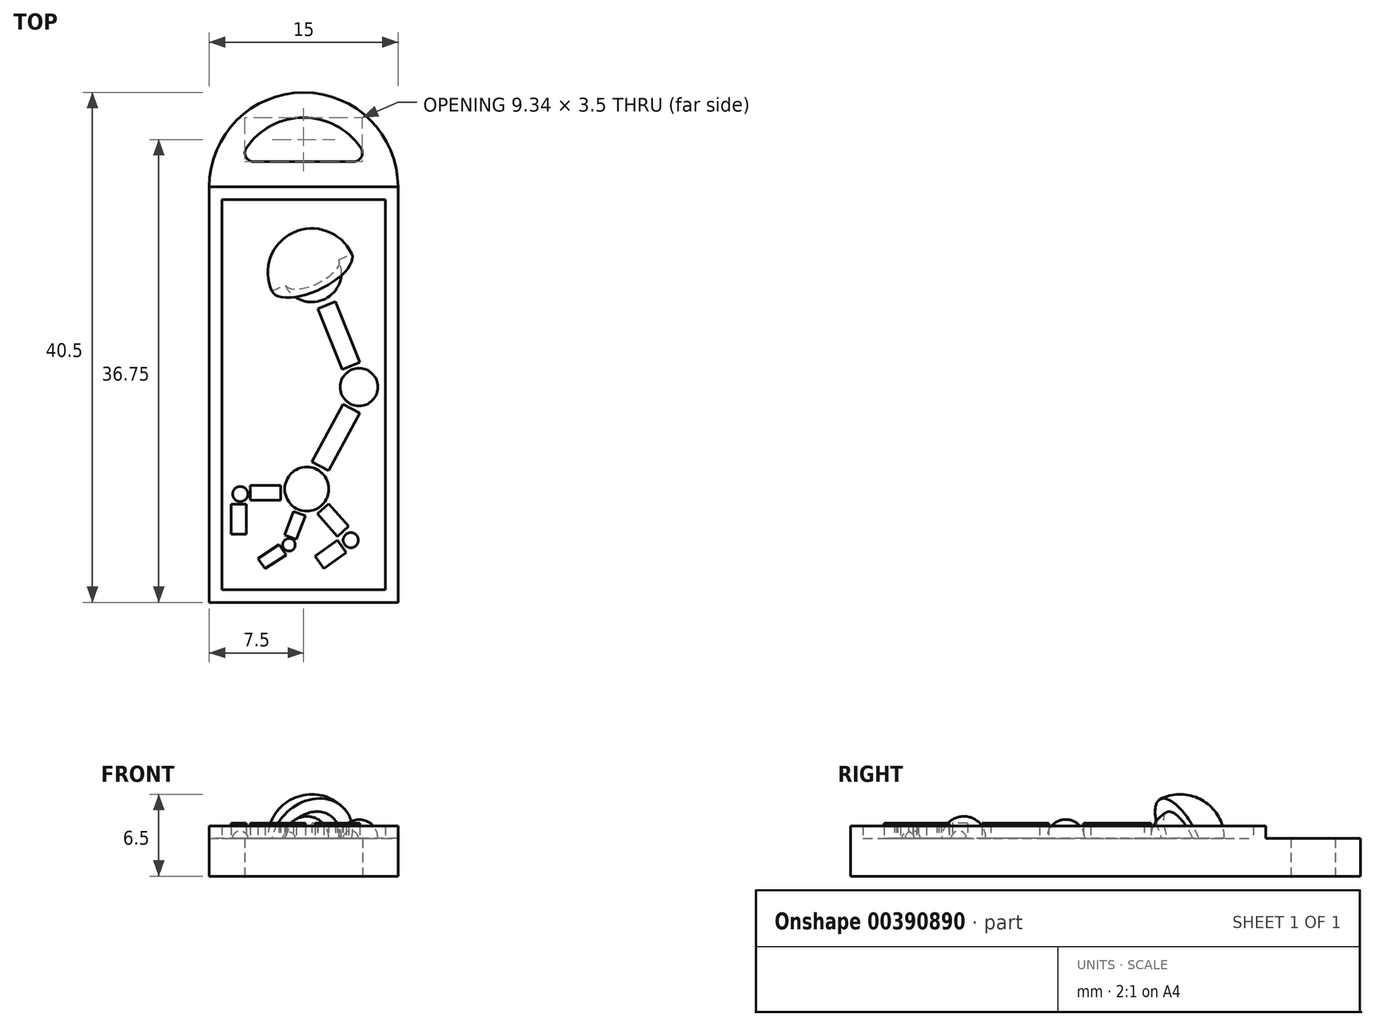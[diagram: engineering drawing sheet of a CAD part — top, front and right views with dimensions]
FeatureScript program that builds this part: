
annotation { "Feature Type Name" : "Feature", "Feature Type Description" : "" }
export const myFeature = defineFeature(function(context is Context, id is Id, definition is map)
    precondition{}
    {
        {
            var Q0;
            Q0=qCreatedBy(makeId("Top.planeOp"),FACE);
            var sketch = newSketch(context, id + "F0", { "sketchPlane" : qUnion([Q0])});
            skLineSegment(sketch, "E0.bottom", {"start": v(0, 0) * mm, "end": v(15, 0) * mm});
            skLineSegment(sketch, "E0.top", {"start": v(0, 33) * mm, "end": v(15, 33) * mm});
            skLineSegment(sketch, "E0.left", {"start": v(0, 0) * mm, "end": v(0, 33) * mm});
            skLineSegment(sketch, "E0.right", {"start": v(15, 0) * mm, "end": v(15, 33) * mm});
            skArc(sketch, "E1", {"start": v(15, 33) * mm, "mid": v(7.5, 40.5) * mm, "end": v(0, 33) * mm});
            skPoint(sketch, "E1.third.point", {"position": v(7.5, 40.5) * mm});
            skPoint(sketch, "E1.third.point.positionSnap0", {"position": v(7.5, 33) * mm});
            skLineSegment(sketch, "E2.0", {"start": v(3.53, 35) * mm, "end": v(11.47, 35) * mm});
            skArc(sketch, "E2.1", {"start": v(12.05, 36.1) * mm, "mid": v(7.5, 38.5) * mm, "end": v(2.95, 36.1) * mm});
            skPoint(sketch, "E3.visualSharp", {"position": v(2.38, 35) * mm});
            skArc(sketch, "E3.filletArc", {"start": v(2.95, 36.1) * mm, "mid": v(2.91, 35.37) * mm, "end": v(3.53, 35) * mm});
            skPoint(sketch, "E4.visualSharp", {"position": v(12.62, 35) * mm});
            skArc(sketch, "E4.filletArc", {"start": v(11.47, 35) * mm, "mid": v(12.09, 35.37) * mm, "end": v(12.05, 36.1) * mm});
            skSolve(sketch);
        }
        {
            var Q0;
            Q0 = qSketchRegion(id + "F0", true);
            extrude(context, id + "F1", {"entities" : qUnion([Q0]), "depth" : 3 * mm});
        }
        {
            var Q0;
            Q0=makeQuery(id+"F1.opExtrude","CAP_FACE",FACE,{"disambiguationData":[OSD([sQuery(id+"F0.wireOp",EDGE,"E0.bottom"),sQuery(id+"F0.wireOp",EDGE,"E0.left"),sQuery(id+"F0.wireOp",EDGE,"E0.right"),sQuery(id+"F0.wireOp",EDGE,"E1"),sQuery(id+"F0.wireOp",EDGE,"E2.0"),sQuery(id+"F0.wireOp",EDGE,"E2.1")])],"isStart":false});
            var sketch = newSketch(context, id + "F2", { "sketchPlane" : qUnion([Q0])});
            skLineSegment(sketch, "E5.bottom", {"start": v(0, 0) * mm, "end": v(15, 0) * mm});
            skLineSegment(sketch, "E5.top", {"start": v(0, 33) * mm, "end": v(15, 33) * mm});
            skLineSegment(sketch, "E5.left", {"start": v(0, 0) * mm, "end": v(0, 33) * mm});
            skLineSegment(sketch, "E5.right", {"start": v(15, 0) * mm, "end": v(15, 33) * mm});
            skLineSegment(sketch, "E6.0", {"start": v(1, 32) * mm, "end": v(14, 32) * mm});
            skLineSegment(sketch, "E6.1", {"start": v(1, 1) * mm, "end": v(1, 32) * mm});
            skLineSegment(sketch, "E6.2", {"start": v(1, 1) * mm, "end": v(14, 1) * mm});
            skLineSegment(sketch, "E6.3", {"start": v(14, 1) * mm, "end": v(14, 32) * mm});
            skSolve(sketch);
        }
        {
            var Q0;
            Q0=makeQuery(id+"FeQCn2nTTUWeUnI_1.boolean.opBoolean","SPLIT",FACE,{"disambiguationData":[TD([makeQuery(id+"FeQCn2nTTUWeUnI_1.opExtrude","SWEPT_FACE",FACE,{"disambiguationData":[OSD([sQuery(id+"F2.wireOp",EDGE,"E6.0")])]})])],"derivedFrom":makeQuery(id+"F1.opExtrude","CAP_FACE",FACE,{"disambiguationData":[OSD([sQuery(id+"F0.wireOp",EDGE,"E0.bottom"),sQuery(id+"F0.wireOp",EDGE,"E0.left"),sQuery(id+"F0.wireOp",EDGE,"E0.right"),sQuery(id+"F0.wireOp",EDGE,"E1"),sQuery(id+"F0.wireOp",EDGE,"E2.0"),sQuery(id+"F0.wireOp",EDGE,"E2.1")])],"isStart":false})});
            var sketch = newSketch(context, id + "F3", { "sketchPlane" : qUnion([Q0])});
            skLineSegment(sketch, "E7", {"start": v(6.7, 35) * mm, "end": v(6.7, 35) * mm});
            skCircle(sketch, "E8", {"center": v(7.72, 9) * mm, "radius": 1.75 * mm});
            skLineSegment(sketch, "E9.bottom", {"start": v(5.67, 9.3) * mm, "end": v(3.27, 9.3) * mm});
            skLineSegment(sketch, "E9.top", {"start": v(5.67, 8.1) * mm, "end": v(3.27, 8.1) * mm});
            skLineSegment(sketch, "E9.left", {"start": v(5.67, 9.3) * mm, "end": v(5.67, 8.1) * mm});
            skLineSegment(sketch, "E9.right", {"start": v(3.27, 9.3) * mm, "end": v(3.27, 8.1) * mm});
            skLineSegment(sketch, "E10", {"start": v(1.73, 7.8) * mm, "end": v(2.93, 7.8) * mm});
            skLineSegment(sketch, "E11", {"start": v(2.93, 7.8) * mm, "end": v(2.93, 5.4) * mm});
            skLineSegment(sketch, "E12", {"start": v(2.93, 5.4) * mm, "end": v(1.73, 5.4) * mm});
            skLineSegment(sketch, "E13", {"start": v(1.73, 5.4) * mm, "end": v(1.73, 7.8) * mm});
            skLineSegment(sketch, "E14", {"start": v(8.6, 7.03) * mm, "end": v(9.5, 7.83) * mm});
            skLineSegment(sketch, "E15", {"start": v(9.5, 7.83) * mm, "end": v(11.09, 6.04) * mm});
            skLineSegment(sketch, "E16", {"start": v(11.09, 6.04) * mm, "end": v(10.19, 5.24) * mm});
            skLineSegment(sketch, "E17", {"start": v(10.19, 5.24) * mm, "end": v(8.6, 7.03) * mm});
            skLineSegment(sketch, "E18", {"start": v(10.89, 3.96) * mm, "end": v(9.1, 2.68) * mm});
            skLineSegment(sketch, "E19", {"start": v(8.4, 3.66) * mm, "end": v(9.1, 2.68) * mm});
            skLineSegment(sketch, "E20", {"start": v(8.4, 3.66) * mm, "end": v(10.19, 4.94) * mm});
            skLineSegment(sketch, "E21", {"start": v(10.89, 3.96) * mm, "end": v(10.19, 4.94) * mm});
            skLineSegment(sketch, "E22", {"start": v(6.7, 7.22) * mm, "end": v(7.64, 6.86) * mm});
            skLineSegment(sketch, "E23", {"start": v(7.64, 6.86) * mm, "end": v(6.93, 5) * mm});
            skLineSegment(sketch, "E24", {"start": v(6.93, 5) * mm, "end": v(6, 5.35) * mm});
            skLineSegment(sketch, "E25", {"start": v(6, 5.35) * mm, "end": v(6.7, 7.22) * mm});
            skLineSegment(sketch, "E26", {"start": v(5.56, 4.6) * mm, "end": v(6.1, 3.76) * mm});
            skLineSegment(sketch, "E27", {"start": v(6.1, 3.76) * mm, "end": v(4.43, 2.67) * mm});
            skLineSegment(sketch, "E28", {"start": v(4.43, 2.67) * mm, "end": v(3.86, 3.49) * mm});
            skLineSegment(sketch, "E29", {"start": v(3.86, 3.49) * mm, "end": v(5.56, 4.6) * mm});
            skSolve(sketch);
        }
        {
            var Q0;
            Q0=makeQuery(id+"F3.imprint","IMPRINT",FACE,{"disambiguationData":[TD([[makeQuery(id+"F3.imprint","IMPRINT",EDGE,{"derivedFrom":sQuery(id+"F3.wireOp",EDGE,"E9.bottom")}),1.0]])]});
            var Q1;
            Q1=makeQuery(id+"F3.imprint","IMPRINT",FACE,{"disambiguationData":[TD([[makeQuery(id+"F3.imprint","IMPRINT",EDGE,{"derivedFrom":sQuery(id+"F3.wireOp",EDGE,"E10")}),-1.0]])]});
            var Q2;
            Q2=makeQuery(id+"F3.imprint","IMPRINT",FACE,{"disambiguationData":[TD([[makeQuery(id+"F3.imprint","IMPRINT",EDGE,{"derivedFrom":sQuery(id+"F3.wireOp",EDGE,"E22")}),-1.0]])]});
            var Q3;
            Q3=makeQuery(id+"F3.imprint","IMPRINT",FACE,{"disambiguationData":[TD([[makeQuery(id+"F3.imprint","IMPRINT",EDGE,{"derivedFrom":sQuery(id+"F3.wireOp",EDGE,"E26")}),-1.0]])]});
            var Q4;
            Q4=makeQuery(id+"F3.imprint","IMPRINT",FACE,{"disambiguationData":[TD([[makeQuery(id+"F3.imprint","IMPRINT",EDGE,{"derivedFrom":sQuery(id+"F3.wireOp",EDGE,"E14")}),-1.0]])]});
            var Q5;
            Q5=makeQuery(id+"F3.imprint","IMPRINT",FACE,{"disambiguationData":[TD([[makeQuery(id+"F3.imprint","IMPRINT",EDGE,{"derivedFrom":sQuery(id+"F3.wireOp",EDGE,"E18")}),-1.0]])]});
            extrude(context, id + "F4", {"entities" : qUnion([Q0, Q1, Q2, Q3, Q4, Q5]), "operationType" : NewBodyOperationType.ADD, "depth" : 1.2 * mm});
        }
        {
            var Q0;
            Q0=makeQuery(id+"FeQCn2nTTUWeUnI_1.boolean.opBoolean","SPLIT",FACE,{"disambiguationData":[TD([makeQuery(id+"FeQCn2nTTUWeUnI_1.opExtrude","SWEPT_FACE",FACE,{"disambiguationData":[OSD([sQuery(id+"F2.wireOp",EDGE,"E6.0")])]})])],"derivedFrom":makeQuery(id+"F1.opExtrude","CAP_FACE",FACE,{"disambiguationData":[OSD([sQuery(id+"F0.wireOp",EDGE,"E0.bottom"),sQuery(id+"F0.wireOp",EDGE,"E0.left"),sQuery(id+"F0.wireOp",EDGE,"E0.right"),sQuery(id+"F0.wireOp",EDGE,"E1"),sQuery(id+"F0.wireOp",EDGE,"E2.0"),sQuery(id+"F0.wireOp",EDGE,"E2.1")])],"isStart":false})});
            var sketch = newSketch(context, id + "F5", { "sketchPlane" : qUnion([Q0])});
            skArc(sketch, "E30", {"start": v(7.75, 7.25) * mm, "mid": v(9.5, 9) * mm, "end": v(7.75, 10.75) * mm});
            skLineSegment(sketch, "E31", {"start": v(7.75, 33.93) * mm, "end": v(7.75, 10.75) * mm, "construction": true});
            skLineSegment(sketch, "E32", {"start": v(7.75, 7.25) * mm, "end": v(7.75, 10.75) * mm});
            skLineSegment(sketch, "E33.trimOffspring", {"start": v(7.75, 7.25) * mm, "end": v(7.75, 0) * mm, "construction": true});
            skSolve(sketch);
        }
        {
            var Q0;
            Q0=makeQuery(id+"FeQCn2nTTUWeUnI_1.boolean.opBoolean","SPLIT",FACE,{"disambiguationData":[TD([makeQuery(id+"FeQCn2nTTUWeUnI_1.opExtrude","SWEPT_FACE",FACE,{"disambiguationData":[OSD([sQuery(id+"F2.wireOp",EDGE,"E6.0")])]})])],"derivedFrom":makeQuery(id+"F1.opExtrude","CAP_FACE",FACE,{"disambiguationData":[OSD([sQuery(id+"F0.wireOp",EDGE,"E0.bottom"),sQuery(id+"F0.wireOp",EDGE,"E0.left"),sQuery(id+"F0.wireOp",EDGE,"E0.right"),sQuery(id+"F0.wireOp",EDGE,"E1"),sQuery(id+"F0.wireOp",EDGE,"E2.0"),sQuery(id+"F0.wireOp",EDGE,"E2.1")])],"isStart":false})});
            var sketch = newSketch(context, id + "F6", { "sketchPlane" : qUnion([Q0])});
            skLineSegment(sketch, "E34", {"start": v(11.96, 15.02) * mm, "end": v(10.64, 15.74) * mm});
            skLineSegment(sketch, "E35", {"start": v(10.64, 15.74) * mm, "end": v(8.17, 11.16) * mm});
            skLineSegment(sketch, "E36", {"start": v(11.96, 15.02) * mm, "end": v(9.49, 10.45) * mm});
            skLineSegment(sketch, "E37", {"start": v(9.49, 10.45) * mm, "end": v(8.17, 11.16) * mm});
            skCircle(sketch, "E38", {"center": v(11.9, 17.1) * mm, "radius": 1.5 * mm});
            skLineSegment(sketch, "E39", {"start": v(7.5, 35) * mm, "end": v(7.5, 0) * mm, "construction": true});
            skLineSegment(sketch, "E40", {"start": v(10.58, 18.5) * mm, "end": v(11.97, 19.07) * mm});
            skLineSegment(sketch, "E41", {"start": v(11.97, 19.07) * mm, "end": v(10.02, 23.9) * mm});
            skLineSegment(sketch, "E42", {"start": v(10.02, 23.9) * mm, "end": v(8.63, 23.33) * mm});
            skLineSegment(sketch, "E43", {"start": v(8.63, 23.33) * mm, "end": v(10.58, 18.5) * mm});
            skSolve(sketch);
        }
        {
            var Q0;
            Q0=makeQuery(id+"F6.imprint","IMPRINT",FACE,{"disambiguationData":[TD([[makeQuery(id+"F6.imprint","IMPRINT",EDGE,{"derivedFrom":sQuery(id+"F6.wireOp",EDGE,"E40")}),1.0]])]});
            var Q1;
            Q1=makeQuery(id+"F6.imprint","IMPRINT",FACE,{"disambiguationData":[TD([[makeQuery(id+"F6.imprint","IMPRINT",EDGE,{"derivedFrom":sQuery(id+"F6.wireOp",EDGE,"E34")}),1.0]])]});
            extrude(context, id + "F7", {"entities" : qUnion([Q0, Q1]), "operationType" : NewBodyOperationType.ADD, "depth" : 1.2 * mm});
        }
        {
            var Q0;
            Q0=makeQuery(id+"FeQCn2nTTUWeUnI_1.boolean.opBoolean","SPLIT",FACE,{"disambiguationData":[TD([makeQuery(id+"FeQCn2nTTUWeUnI_1.opExtrude","SWEPT_FACE",FACE,{"disambiguationData":[OSD([sQuery(id+"F2.wireOp",EDGE,"E6.0")])]})])],"derivedFrom":makeQuery(id+"F1.opExtrude","CAP_FACE",FACE,{"disambiguationData":[OSD([sQuery(id+"F0.wireOp",EDGE,"E0.bottom"),sQuery(id+"F0.wireOp",EDGE,"E0.left"),sQuery(id+"F0.wireOp",EDGE,"E0.right"),sQuery(id+"F0.wireOp",EDGE,"E1"),sQuery(id+"F0.wireOp",EDGE,"E2.0"),sQuery(id+"F0.wireOp",EDGE,"E2.1")])],"isStart":false})});
            var sketch = newSketch(context, id + "F8", { "sketchPlane" : qUnion([Q0])});
            skArc(sketch, "E44", {"start": v(11.9, 15.6) * mm, "mid": v(13.4, 17.1) * mm, "end": v(11.9, 18.6) * mm});
            skPoint(sketch, "E44.centerSnap0", {"position": v(11.9, 17.18) * mm});
            skLineSegment(sketch, "E45", {"start": v(11.9, 15.6) * mm, "end": v(11.9, 18.6) * mm});
            skSolve(sketch);
        }
        {
            var Q0;
            Q0 = qSketchRegion(id + "F8", true);
            var Q1;
            Q1=sQuery(id+"F8.wireOp",EDGE,"E45");
            revolve(context, id + "F9", {"operationType" : NewBodyOperationType.ADD, "entities" : qUnion([Q0]), "axis" : qUnion([Q1]), "revolveType" : RevolveType.ONE_DIRECTION, "oppositeDirection" : true, "angle" : 180 * degree});
        }
        {
            var Q0;
            Q0=makeQuery(id+"FeQCn2nTTUWeUnI_1.boolean.opBoolean","SPLIT",FACE,{"disambiguationData":[TD([makeQuery(id+"FeQCn2nTTUWeUnI_1.opExtrude","SWEPT_FACE",FACE,{"disambiguationData":[OSD([sQuery(id+"F2.wireOp",EDGE,"E6.0")])]})])],"derivedFrom":makeQuery(id+"F1.opExtrude","CAP_FACE",FACE,{"disambiguationData":[OSD([sQuery(id+"F0.wireOp",EDGE,"E0.bottom"),sQuery(id+"F0.wireOp",EDGE,"E0.left"),sQuery(id+"F0.wireOp",EDGE,"E0.right"),sQuery(id+"F0.wireOp",EDGE,"E1"),sQuery(id+"F0.wireOp",EDGE,"E2.0"),sQuery(id+"F0.wireOp",EDGE,"E2.1")])],"isStart":false})});
            var sketch = newSketch(context, id + "F10", { "sketchPlane" : qUnion([Q0])});
            skArc(sketch, "E46", {"start": v(8.15, 23.85) * mm, "mid": v(10.5, 26.2) * mm, "end": v(8.15, 28.55) * mm});
            skLineSegment(sketch, "E47", {"start": v(8.15, 23.85) * mm, "end": v(8.15, 28.55) * mm});
            skSolve(sketch);
        }
        {
            var Q0;
            Q0 = qSketchRegion(id + "F10", true);
            var Q1;
            Q1=sQuery(id+"F10.wireOp",EDGE,"E47");
            revolve(context, id + "F11", {"operationType" : NewBodyOperationType.ADD, "entities" : qUnion([Q0]), "axis" : qUnion([Q1]), "revolveType" : RevolveType.ONE_DIRECTION, "oppositeDirection" : true, "angle" : 180 * degree});
        }
        {
            var Q0;
            Q0=makeQuery(id+"FeQCn2nTTUWeUnI_1.boolean.opBoolean","SPLIT",FACE,{"disambiguationData":[TD([makeQuery(id+"FeQCn2nTTUWeUnI_1.opExtrude","SWEPT_FACE",FACE,{"disambiguationData":[OSD([sQuery(id+"F2.wireOp",EDGE,"E6.0")])]})])],"derivedFrom":makeQuery(id+"F1.opExtrude","CAP_FACE",FACE,{"disambiguationData":[OSD([sQuery(id+"F0.wireOp",EDGE,"E0.bottom"),sQuery(id+"F0.wireOp",EDGE,"E0.left"),sQuery(id+"F0.wireOp",EDGE,"E0.right"),sQuery(id+"F0.wireOp",EDGE,"E1"),sQuery(id+"F0.wireOp",EDGE,"E2.0"),sQuery(id+"F0.wireOp",EDGE,"E2.1")])],"isStart":false})});
            var sketch = newSketch(context, id + "F12", { "sketchPlane" : qUnion([Q0])});
            skArc(sketch, "E48.converted", {"start": v(11.32, 27.68) * mm, "mid": v(6.67, 29.37) * mm, "end": v(4.98, 24.72) * mm});
            skLineSegment(sketch, "E49", {"start": v(4.98, 24.72) * mm, "end": v(11.32, 27.68) * mm});
            skSolve(sketch);
        }
        {
            var Q0;
            Q0=makeQuery(id+"FeQCn2nTTUWeUnI_1.boolean.opBoolean","SPLIT",FACE,{"disambiguationData":[TD([makeQuery(id+"FeQCn2nTTUWeUnI_1.opExtrude","SWEPT_FACE",FACE,{"disambiguationData":[OSD([sQuery(id+"F2.wireOp",EDGE,"E6.0")])]})])],"derivedFrom":makeQuery(id+"F1.opExtrude","CAP_FACE",FACE,{"disambiguationData":[OSD([sQuery(id+"F0.wireOp",EDGE,"E0.bottom"),sQuery(id+"F0.wireOp",EDGE,"E0.left"),sQuery(id+"F0.wireOp",EDGE,"E0.right"),sQuery(id+"F0.wireOp",EDGE,"E1"),sQuery(id+"F0.wireOp",EDGE,"E2.0"),sQuery(id+"F0.wireOp",EDGE,"E2.1")])],"isStart":false})});
            var sketch = newSketch(context, id + "F13", { "sketchPlane" : qUnion([Q0])});
            skArc(sketch, "E50", {"start": v(2.57, 8) * mm, "mid": v(3.07, 8.5) * mm, "end": v(2.57, 9) * mm});
            skArc(sketch, "E51", {"start": v(11.24, 4.34) * mm, "mid": v(11.84, 4.94) * mm, "end": v(11.24, 5.54) * mm});
            skArc(sketch, "E52", {"start": v(6.33, 4.07) * mm, "mid": v(6.83, 4.57) * mm, "end": v(6.33, 5.07) * mm});
            skLineSegment(sketch, "E53", {"start": v(2.57, 8) * mm, "end": v(2.57, 9) * mm});
            skLineSegment(sketch, "E54", {"start": v(6.33, 5.07) * mm, "end": v(6.33, 4.07) * mm});
            skLineSegment(sketch, "E55", {"start": v(11.24, 5.54) * mm, "end": v(11.24, 4.34) * mm});
            skSolve(sketch);
        }
        {
            var Q0;
            Q0=makeQuery(id+"FeQCn2nTTUWeUnI_1.boolean.opBoolean","SPLIT",FACE,{"disambiguationData":[TD([makeQuery(id+"FeQCn2nTTUWeUnI_1.opExtrude","SWEPT_FACE",FACE,{"disambiguationData":[OSD([sQuery(id+"F2.wireOp",EDGE,"E6.0")])]})])],"derivedFrom":makeQuery(id+"F1.opExtrude","CAP_FACE",FACE,{"disambiguationData":[OSD([sQuery(id+"F0.wireOp",EDGE,"E0.bottom"),sQuery(id+"F0.wireOp",EDGE,"E0.left"),sQuery(id+"F0.wireOp",EDGE,"E0.right"),sQuery(id+"F0.wireOp",EDGE,"E1"),sQuery(id+"F0.wireOp",EDGE,"E2.0"),sQuery(id+"F0.wireOp",EDGE,"E2.1")])],"isStart":false})});
            var sketch = newSketch(context, id + "F14", { "sketchPlane" : qUnion([Q0])});
            skArc(sketch, "E56.converted", {"start": v(2.47, 8) * mm, "mid": v(3.07, 8.6) * mm, "end": v(2.47, 9.2) * mm});
            skLineSegment(sketch, "E57", {"start": v(2.47, 8) * mm, "end": v(2.47, 9.2) * mm});
            skSolve(sketch);
        }
        {
            var Q0;
            Q0 = qSketchRegion(id + "F14", true);
            var Q1;
            Q1=sQuery(id+"F14.wireOp",EDGE,"E57");
            revolve(context, id + "F15", {"operationType" : NewBodyOperationType.ADD, "entities" : qUnion([Q0]), "axis" : qUnion([Q1]), "revolveType" : RevolveType.ONE_DIRECTION, "oppositeDirection" : true, "angle" : 180 * degree});
        }
        {
            var Q0;
            Q0=makeQuery(id+"F13.imprint","IMPRINT",FACE,{"disambiguationData":[TD([[makeQuery(id+"F13.imprint","IMPRINT",EDGE,{"derivedFrom":sQuery(id+"F13.wireOp",EDGE,"E52")}),1.0]])]});
            var Q1;
            Q1=sQuery(id+"F13.wireOp",EDGE,"E54");
            revolve(context, id + "F16", {"operationType" : NewBodyOperationType.ADD, "entities" : qUnion([Q0]), "axis" : qUnion([Q1]), "revolveType" : RevolveType.ONE_DIRECTION, "angle" : 180 * degree});
        }
        {
            var Q0;
            Q0=makeQuery(id+"FeQCn2nTTUWeUnI_1.boolean.opBoolean","SPLIT",FACE,{"disambiguationData":[TD([makeQuery(id+"FeQCn2nTTUWeUnI_1.opExtrude","SWEPT_FACE",FACE,{"disambiguationData":[OSD([sQuery(id+"F2.wireOp",EDGE,"E6.0")])]})])],"derivedFrom":makeQuery(id+"F1.opExtrude","CAP_FACE",FACE,{"disambiguationData":[OSD([sQuery(id+"F0.wireOp",EDGE,"E0.bottom"),sQuery(id+"F0.wireOp",EDGE,"E0.left"),sQuery(id+"F0.wireOp",EDGE,"E0.right"),sQuery(id+"F0.wireOp",EDGE,"E1"),sQuery(id+"F0.wireOp",EDGE,"E2.0"),sQuery(id+"F0.wireOp",EDGE,"E2.1")])],"isStart":false})});
            var sketch = newSketch(context, id + "F17", { "sketchPlane" : qUnion([Q0])});
            skArc(sketch, "E58", {"start": v(11.24, 4.34) * mm, "mid": v(11.84, 4.94) * mm, "end": v(11.24, 5.54) * mm});
            skLineSegment(sketch, "E59", {"start": v(11.24, 5.54) * mm, "end": v(11.24, 4.34) * mm});
            skSolve(sketch);
        }
        {
            var Q0;
            Q0 = qSketchRegion(id + "F17", true);
            var Q1;
            Q1=sQuery(id+"F17.wireOp",EDGE,"E59");
            revolve(context, id + "F18", {"operationType" : NewBodyOperationType.ADD, "entities" : qUnion([Q0]), "axis" : qUnion([Q1]), "revolveType" : RevolveType.ONE_DIRECTION, "angle" : 180 * degree});
        }
        {
            var Q0;
            Q0 = qSketchRegion(id + "F12", true);
            var Q1;
            Q1=sQuery(id+"F12.wireOp",EDGE,"E49");
            revolve(context, id + "F19", {"operationType" : NewBodyOperationType.ADD, "entities" : qUnion([Q0]), "axis" : qUnion([Q1]), "revolveType" : RevolveType.ONE_DIRECTION, "angle" : 115 * degree});
        }
        {
            var Q0;
            {var subQ0=sQuery(id+"F5.wireOp",EDGE,"E30");Q0=makeQuery(id+"F5.imprint","IMPRINT",FACE,{"disambiguationData":[TD([[makeQuery(id+"F5.imprint","IMPRINT",EDGE,{"derivedFrom":subQ0}),1.0]])]});}
            var Q1;
            Q1=sQuery(id+"F5.wireOp",EDGE,"E32");
            revolve(context, id + "F20", {"operationType" : NewBodyOperationType.ADD, "entities" : qUnion([Q0]), "axis" : qUnion([Q1]), "revolveType" : RevolveType.ONE_DIRECTION, "oppositeDirection" : true, "angle" : 180 * degree});
        }
        {
            var Q0;
            Q0 = qSketchRegion(id + "F2", true);
            extrude(context, id + "F21", {"entities" : qUnion([Q0]), "operationType" : NewBodyOperationType.ADD, "depth" : 1 * mm});
        }
    });
